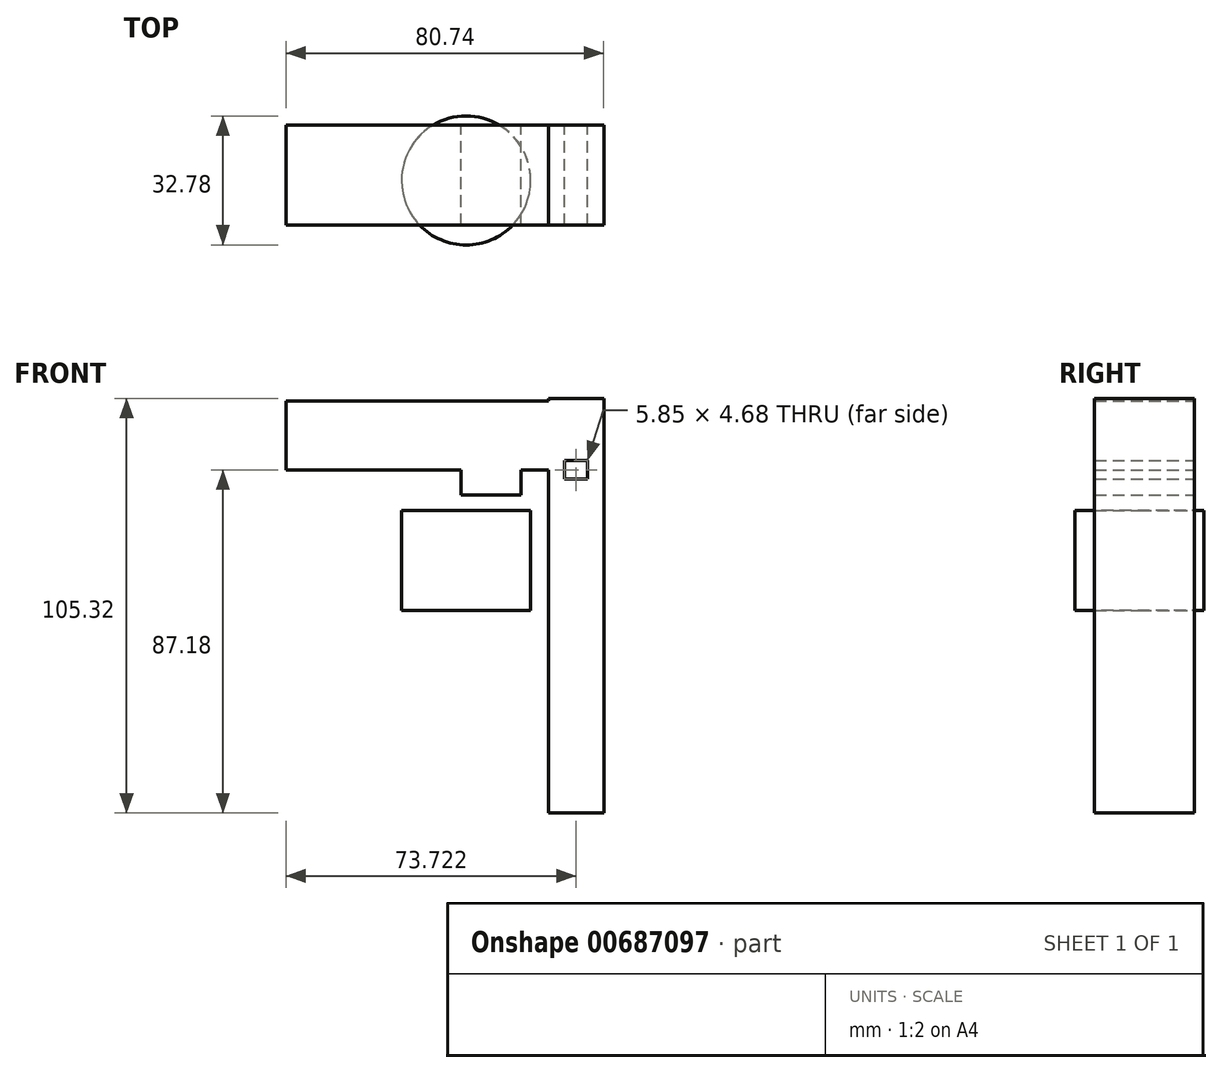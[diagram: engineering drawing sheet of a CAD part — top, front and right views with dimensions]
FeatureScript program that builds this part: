
annotation { "Feature Type Name" : "Feature", "Feature Type Description" : "" }
export const myFeature = defineFeature(function(context is Context, id is Id, definition is map)
    precondition{}
    {
        {
            var Q0;
            Q0=qCreatedBy(makeId("Front.planeOp"),FACE);
            var sketch = newSketch(context, id + "F0", { "sketchPlane" : qUnion([Q0])});
            skLineSegment(sketch, "E0.bottom", {"start": v(-31.45, 35.7) * mm, "end": v(-105.17, 35.7) * mm});
            skLineSegment(sketch, "E0.top", {"start": v(-31.45, 53.24) * mm, "end": v(-105.17, 53.24) * mm});
            skLineSegment(sketch, "E0.left", {"start": v(-31.45, 35.7) * mm, "end": v(-31.45, 53.24) * mm});
            skLineSegment(sketch, "E0.right", {"start": v(-105.17, 35.7) * mm, "end": v(-105.17, 53.24) * mm});
            skPoint(sketch, "E0.middle", {"position": v(-68.3, 44.47) * mm});
            skLineSegment(sketch, "E1.bottom", {"start": v(-45.5, 29.25) * mm, "end": v(-60.7, 29.25) * mm});
            skLineSegment(sketch, "E1.top", {"start": v(-45.5, 42.13) * mm, "end": v(-60.7, 42.13) * mm});
            skLineSegment(sketch, "E1.left", {"start": v(-45.5, 29.25) * mm, "end": v(-45.5, 42.13) * mm});
            skLineSegment(sketch, "E1.right", {"start": v(-60.7, 29.25) * mm, "end": v(-60.7, 42.13) * mm});
            skPoint(sketch, "E1.middle", {"position": v(-53.1, 35.7) * mm});
            skLineSegment(sketch, "E2.bottom", {"start": v(-24.43, 17.55) * mm, "end": v(-38.47, 17.55) * mm});
            skLineSegment(sketch, "E2.top", {"start": v(-24.43, 53.83) * mm, "end": v(-38.47, 53.83) * mm});
            skLineSegment(sketch, "E2.left", {"start": v(-24.43, 17.55) * mm, "end": v(-24.43, 53.83) * mm});
            skLineSegment(sketch, "E2.right", {"start": v(-38.47, 17.55) * mm, "end": v(-38.47, 53.83) * mm});
            skPoint(sketch, "E2.middle", {"position": v(-31.45, 35.7) * mm});
            skLineSegment(sketch, "E3.bottom", {"start": v(-38.47, 17.55) * mm, "end": v(-24.43, 17.55) * mm});
            skLineSegment(sketch, "E3.top", {"start": v(-38.47, -51.49) * mm, "end": v(-24.43, -51.49) * mm});
            skLineSegment(sketch, "E3.left", {"start": v(-38.47, 17.55) * mm, "end": v(-38.47, -51.49) * mm});
            skLineSegment(sketch, "E3.right", {"start": v(-24.43, 17.55) * mm, "end": v(-24.43, -51.49) * mm});
            skPoint(sketch, "E3.middle", {"position": v(-31.45, -16.97) * mm});
            skLineSegment(sketch, "E4.bottom", {"start": v(-28.52, 33.35) * mm, "end": v(-34.37, 33.35) * mm});
            skLineSegment(sketch, "E4.top", {"start": v(-28.52, 38.03) * mm, "end": v(-34.37, 38.03) * mm});
            skLineSegment(sketch, "E4.left", {"start": v(-28.52, 33.35) * mm, "end": v(-28.52, 38.03) * mm});
            skLineSegment(sketch, "E4.right", {"start": v(-34.37, 33.35) * mm, "end": v(-34.37, 38.03) * mm});
            skSolve(sketch);
        }
        {
            var Q0;
            Q0 = qSketchRegion(id + "F0", true);
            extrude(context, id + "F1", {"entities" : qUnion([Q0]), "depth" : 25.4 * mm, "offsetDistance" : 25.4 * mm});
        }
        {
            var Q0;
            Q0=qCreatedBy(makeId("Top.planeOp"),FACE);
            var sketch = newSketch(context, id + "F2", { "sketchPlane" : qUnion([Q0])});
            skCircle(sketch, "E5", {"center": v(-59.39, -14.04) * mm, "radius": 16.4 * mm});
            skSolve(sketch);
        }
        {
            var Q0;
            Q0 = qSketchRegion(id + "F2", true);
            extrude(context, id + "F3", {"entities" : qUnion([Q0]), "depth" : 25.4 * mm, "offsetDistance" : 25.4 * mm});
        }
    });
